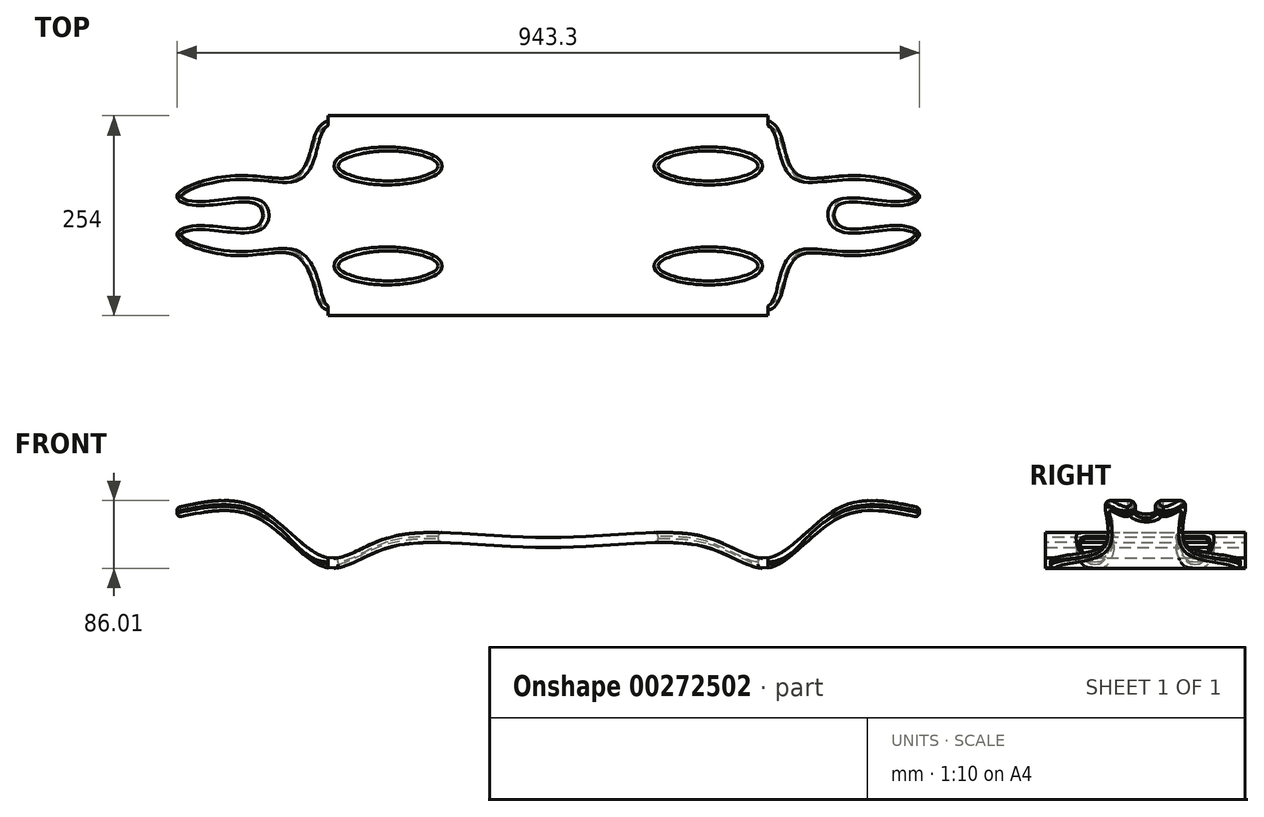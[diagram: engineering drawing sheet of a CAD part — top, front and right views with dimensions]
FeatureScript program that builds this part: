
annotation { "Feature Type Name" : "Feature", "Feature Type Description" : "" }
export const myFeature = defineFeature(function(context is Context, id is Id, definition is map)
    precondition{}
    {
        {
            var Q0;
            Q0=qCreatedBy(makeId("Front.planeOp"),FACE);
            var sketch = newSketch(context, id + "F0", { "sketchPlane" : qUnion([Q0])});
            skPoint(sketch, "E0.middle", {"position": v(0, 0) * mm});
            skLineSegment(sketch, "E1.right", {"start": v(-471.71, 57.15) * mm, "end": v(-471.71, 69.85) * mm});
            skLineSegment(sketch, "E2", {"start": v(-471.71, 69.85) * mm, "end": v(-471.71, 57.15) * mm});
            skLineSegment(sketch, "E3", {"start": v(471.71, 57.15) * mm, "end": v(471.71, 69.85) * mm});
            skPoint(sketch, "E4.endSnap0", {"position": v(0, 6.35) * mm});
            skPoint(sketch, "E4.start.orphan", {"position": v(0, -6.35) * mm});
            skPoint(sketch, "E5.trimOffspring.end.orphan", {"position": v(0, 19.05) * mm});
            skPoint(sketch, "E6.start.orphan", {"position": v(228.6, 19.05) * mm});
            skPoint(sketch, "E7.end.orphan", {"position": v(-228.6, 19.05) * mm});
            skFitSpline(sketch, "E8", {"points": [v(-471.71, 57.15) * mm, v(-370.11, 57.15) * mm, v(-281.21, -6.35) * mm, v(-203.2, 19.05) * mm, v(0, 19.05) * mm, v(203.2, 19.05) * mm, v(281.21, -6.35) * mm, v(370.11, 57.15) * mm, v(471.71, 57.15) * mm], "startDerivative": vector(913.94, 203.4) * mm, "endDerivative": vector(913.94, -203.4) * mm});
            skFitSpline(sketch, "E9", {"points": [v(471.71, 69.85) * mm, v(370.11, 69.85) * mm, v(281.21, 6.35) * mm, v(203.2, 31.75) * mm, v(0, 31.75) * mm, v(-203.2, 31.75) * mm, v(-281.21, 6.35) * mm, v(-370.11, 69.85) * mm, v(-471.71, 69.85) * mm], "startDerivative": vector(-913.94, 203.4) * mm, "endDerivative": vector(-913.94, -203.4) * mm});
            skPoint(sketch, "E0.right.end.orphan", {"position": v(-319.31, -6.35) * mm});
            skPoint(sketch, "E0.right.start.orphan", {"position": v(-319.31, 6.35) * mm});
            skSolve(sketch);
        }
        {
            var Q0;
            Q0 = qSketchRegion(id + "F0", true);
            extrude(context, id + "F1", {"entities" : qUnion([Q0]), "depth" : 127 * mm, "offsetDistance" : 25.4 * mm, "hasSecondDirection" : true, "secondDirectionOppositeDirection" : true, "secondDirectionDepth" : 127 * mm});
        }
        {
            var Q0;
            Q0=qCreatedBy(makeId("Top.planeOp"),FACE);
            var sketch = newSketch(context, id + "F2", { "sketchPlane" : qUnion([Q0])});
            skLineSegment(sketch, "E10.bottom", {"start": v(473.08, 127) * mm, "end": v(-473.07, 127) * mm});
            skLineSegment(sketch, "E10.top", {"start": v(473.07, -127) * mm, "end": v(-473.08, -127) * mm});
            skLineSegment(sketch, "E10.left", {"start": v(473.08, 127) * mm, "end": v(473.08, 50.8) * mm});
            skLineSegment(sketch, "E10.right", {"start": v(-473.08, 127) * mm, "end": v(-473.08, -127) * mm});
            skPoint(sketch, "E10.middle", {"position": v(0, 0) * mm});
            skLineSegment(sketch, "E11", {"start": v(-364.02, 0) * mm, "end": v(369.89, 0) * mm});
            skLineSegment(sketch, "E12", {"start": v(0, 101.2) * mm, "end": v(0, -101.6) * mm});
            skLineSegment(sketch, "E13", {"start": v(-473.08, 50.8) * mm, "end": v(-473.08, -50.8) * mm});
            skLineSegment(sketch, "E14", {"start": v(473.07, -50.8) * mm, "end": v(473.07, 50.8) * mm});
            skLineSegment(sketch, "E15.trimOffspring", {"start": v(473.08, -50.8) * mm, "end": v(473.08, -127) * mm});
            skLineSegment(sketch, "E16.left", {"start": v(473.07, 50.8) * mm, "end": v(473.07, -50.8) * mm});
            skLineSegment(sketch, "E16.right", {"start": v(319.09, 50.8) * mm, "end": v(319.09, -50.8) * mm});
            skLineSegment(sketch, "E17.left", {"start": v(-473.08, -50.8) * mm, "end": v(-473.08, 50.8) * mm});
            skLineSegment(sketch, "E17.right", {"start": v(-320.67, -50.8) * mm, "end": v(-320.67, 50.8) * mm});
            skLineSegment(sketch, "E18", {"start": v(-279.4, -127) * mm, "end": v(279.4, -127) * mm});
            skLineSegment(sketch, "E19.top", {"start": v(-279.4, 127) * mm, "end": v(279.4, 127) * mm});
            skLineSegment(sketch, "E19.left", {"start": v(-279.4, -102) * mm, "end": v(-279.4, 101.2) * mm});
            skLineSegment(sketch, "E19.right", {"start": v(279.4, -120.65) * mm, "end": v(279.4, 101.2) * mm});
            skLineSegment(sketch, "E20", {"start": v(-473.08, 0) * mm, "end": v(-473.08, 50.8) * mm});
            skLineSegment(sketch, "E21", {"start": v(-473.08, 0) * mm, "end": v(-473.08, -50.8) * mm});
            skLineSegment(sketch, "E22", {"start": v(473.07, -50.8) * mm, "end": v(473.07, 0) * mm});
            skLineSegment(sketch, "E23", {"start": v(473.08, 0) * mm, "end": v(473.08, 50.8) * mm});
            skLineSegment(sketch, "E24.left", {"start": v(-473.07, -13.1) * mm, "end": v(-473.08, 12.3) * mm});
            skPoint(sketch, "E24.middle", {"position": v(-420.69, 0) * mm});
            skLineSegment(sketch, "E25.left", {"start": v(473.08, -13.1) * mm, "end": v(471.49, 12.7) * mm});
            skPoint(sketch, "E25.middle", {"position": v(420.69, 0) * mm});
            skPoint(sketch, "E26.end.orphan", {"position": v(0, -127) * mm});
            skPoint(sketch, "E27.end.orphan", {"position": v(0, 127) * mm});
            skLineSegment(sketch, "E28", {"start": v(-279.4, -127) * mm, "end": v(-279.4, -120.65) * mm});
            skLineSegment(sketch, "E29", {"start": v(-279.4, -120.65) * mm, "end": v(-279.4, -127) * mm});
            skLineSegment(sketch, "E30", {"start": v(-279.4, 127) * mm, "end": v(-279.4, 120.65) * mm});
            skLineSegment(sketch, "E31", {"start": v(-279.4, 120.65) * mm, "end": v(-279.4, 127) * mm});
            skLineSegment(sketch, "E32", {"start": v(279.4, 120.65) * mm, "end": v(279.4, 127) * mm});
            skLineSegment(sketch, "E33", {"start": v(279.4, -120.65) * mm, "end": v(279.4, -127) * mm});
            skFitSpline(sketch, "E34", {"points": [v(319.09, -50.8) * mm, v(396.08, -50.8) * mm, v(471.49, -25.4) * mm, v(446.09, -12.7) * mm, v(369.89, -12.7) * mm, v(368.3, 13.1) * mm, v(446.09, 12.7) * mm, v(471.49, 25.4) * mm, v(396.08, 50.8) * mm, v(319.09, 50.8) * mm, v(299.24, 88.9) * mm, v(279.4, 120.65) * mm, v(0, 101.2) * mm, v(-279.4, 120.65) * mm, v(-300.04, 88.9) * mm, v(-320.67, 50.8) * mm, v(-396.88, 50.8) * mm, v(-471.49, 25.4) * mm, v(-446.09, 12.7) * mm, v(-368.3, 13.1) * mm, v(-368.3, -12.3) * mm, v(-446.09, -12.7) * mm, v(-471.49, -25.4) * mm, v(-396.88, -50.8) * mm, v(-320.67, -50.8) * mm, v(-295.64, -95.82) * mm, v(-279.4, -120.65) * mm, v(0, -101.6) * mm, v(279.4, -120.65) * mm, v(299.24, -88.9) * mm, v(319.09, -50.8) * mm]});
            skLineSegment(sketch, "E35.bottom", {"start": v(279.4, 101.2) * mm, "end": v(-279.4, 101.2) * mm});
            skLineSegment(sketch, "E35.top", {"start": v(279.4, -102) * mm, "end": v(-279.4, -102) * mm});
            skLineSegment(sketch, "E35.left", {"start": v(279.4, 101.2) * mm, "end": v(279.4, -102) * mm});
            skLineSegment(sketch, "E35.right", {"start": v(-279.4, 101.2) * mm, "end": v(-279.4, -102) * mm});
            skLineSegment(sketch, "E36.bottom", {"start": v(-279.4, -102) * mm, "end": v(-266.7, -102) * mm});
            skLineSegment(sketch, "E36.top", {"start": v(-279.4, -82.96) * mm, "end": v(-266.7, -82.96) * mm});
            skLineSegment(sketch, "E36.left", {"start": v(-279.4, -102) * mm, "end": v(-279.4, -82.96) * mm});
            skLineSegment(sketch, "E36.right", {"start": v(-266.7, -102) * mm, "end": v(-266.7, -82.96) * mm});
            skLineSegment(sketch, "E37.bottom", {"start": v(-279.4, 101.2) * mm, "end": v(-266.7, 101.2) * mm});
            skLineSegment(sketch, "E37.top", {"start": v(-279.4, 82.14) * mm, "end": v(-266.7, 82.14) * mm});
            skLineSegment(sketch, "E37.left", {"start": v(-279.4, 101.2) * mm, "end": v(-279.4, 82.14) * mm});
            skLineSegment(sketch, "E37.right", {"start": v(-266.7, 101.2) * mm, "end": v(-266.7, 82.14) * mm});
            skLineSegment(sketch, "E38.bottom", {"start": v(279.4, 101.2) * mm, "end": v(266.7, 101.2) * mm});
            skLineSegment(sketch, "E38.top", {"start": v(279.4, 82.14) * mm, "end": v(266.7, 82.14) * mm});
            skLineSegment(sketch, "E38.left", {"start": v(279.4, 101.2) * mm, "end": v(279.4, 82.14) * mm});
            skLineSegment(sketch, "E38.right", {"start": v(266.7, 101.2) * mm, "end": v(266.7, 82.14) * mm});
            skLineSegment(sketch, "E39.bottom", {"start": v(279.4, -102) * mm, "end": v(266.7, -102) * mm});
            skLineSegment(sketch, "E39.top", {"start": v(279.4, -82.96) * mm, "end": v(266.7, -82.96) * mm});
            skLineSegment(sketch, "E39.left", {"start": v(279.4, -102) * mm, "end": v(279.4, -82.96) * mm});
            skLineSegment(sketch, "E39.right", {"start": v(266.7, -102) * mm, "end": v(266.7, -82.96) * mm});
            skLineSegment(sketch, "E40", {"start": v(-266.7, -82.96) * mm, "end": v(-266.7, -44.86) * mm});
            skLineSegment(sketch, "E41", {"start": v(-266.7, 82.14) * mm, "end": v(-266.7, 44.04) * mm});
            skLineSegment(sketch, "E42", {"start": v(266.7, -82.96) * mm, "end": v(266.7, -44.86) * mm});
            skLineSegment(sketch, "E43", {"start": v(266.7, 82.14) * mm, "end": v(266.7, 44.04) * mm});
            skLineSegment(sketch, "E44.bottom", {"start": v(-266.7, -44.86) * mm, "end": v(-139.7, -44.86) * mm});
            skLineSegment(sketch, "E44.top", {"start": v(-266.7, -82.96) * mm, "end": v(-139.7, -82.96) * mm});
            skLineSegment(sketch, "E44.left", {"start": v(-266.7, -44.86) * mm, "end": v(-266.7, -82.96) * mm});
            skLineSegment(sketch, "E44.right", {"start": v(-139.7, -44.86) * mm, "end": v(-139.7, -82.96) * mm});
            skLineSegment(sketch, "E45.bottom", {"start": v(-266.7, 82.14) * mm, "end": v(-139.7, 82.14) * mm});
            skLineSegment(sketch, "E45.top", {"start": v(-266.7, 44.04) * mm, "end": v(-139.7, 44.04) * mm});
            skLineSegment(sketch, "E45.right", {"start": v(-139.7, 82.14) * mm, "end": v(-139.7, 44.04) * mm});
            skLineSegment(sketch, "E46.bottom", {"start": v(266.7, 82.14) * mm, "end": v(139.7, 82.14) * mm});
            skLineSegment(sketch, "E46.top", {"start": v(266.7, 44.04) * mm, "end": v(139.7, 44.04) * mm});
            skLineSegment(sketch, "E46.right", {"start": v(139.7, 82.14) * mm, "end": v(139.7, 44.04) * mm});
            skLineSegment(sketch, "E47.bottom", {"start": v(266.7, -82.96) * mm, "end": v(139.7, -82.96) * mm});
            skLineSegment(sketch, "E47.top", {"start": v(266.7, -44.86) * mm, "end": v(139.7, -44.86) * mm});
            skLineSegment(sketch, "E47.right", {"start": v(139.7, -82.96) * mm, "end": v(139.7, -44.86) * mm});
            skFitSpline(sketch, "E48", {"points": [v(-266.7, 63.1) * mm, v(-203.2, 44.04) * mm, v(-139.7, 63.1) * mm, v(-203.2, 82.14) * mm, v(-266.7, 63.1) * mm]});
            skFitSpline(sketch, "E49", {"points": [v(-266.7, -63.9) * mm, v(-203.2, -82.96) * mm, v(-139.7, -63.9) * mm, v(-203.2, -44.86) * mm, v(-266.7, -63.9) * mm]});
            skFitSpline(sketch, "E50", {"points": [v(139.7, -63.9) * mm, v(203.2, -82.96) * mm, v(266.7, -63.9) * mm, v(203.2, -44.86) * mm, v(139.7, -63.9) * mm]});
            skFitSpline(sketch, "E51", {"points": [v(139.7, 63.1) * mm, v(203.2, 44.04) * mm, v(266.7, 63.1) * mm, v(203.2, 82.14) * mm, v(139.7, 63.1) * mm]});
            skSolve(sketch);
        }
        {
            var Q0;
            {var subQ5=sQuery(id+"F2.wireOp",EDGE,"E15.trimOffspring");Q0=makeQuery(id+"F2.imprint","IMPRINT",FACE,{"disambiguationData":[TD([[makeQuery(id+"F2.imprint","IMPRINT",EDGE,{"derivedFrom":subQ5}),-1.0]])]});}
            var Q1;
            {var subQ4=sQuery(id+"F2.wireOp",EDGE,"E25.left");Q1=makeQuery(id+"F2.imprint","IMPRINT",FACE,{"disambiguationData":[TD([[makeQuery(id+"F2.imprint","IMPRINT",EDGE,{"derivedFrom":subQ4}),1.0]])]});}
            var Q2;
            {var subQ0=sQuery(id+"F2.wireOp",EDGE,"e9d015ac-fda8-45dd-bf0b-8d8da068c592");var subQ1=sQuery(id+"F2.wireOp",EDGE,"E19.top");var subQ2=makeQuery(id+"F2.imprint","INTERSECT",VERTEX,{"disambiguationData":[OD(0.0)],"derivedFrom":[subQ1,subQ0]});Q2=makeQuery(id+"F2.imprint","IMPRINT",FACE,{"disambiguationData":[TD([[makeQuery(id+"F2.imprint","IMPRINT",EDGE,{"disambiguationData":[TD([[subQ2,-1.0]])],"derivedFrom":subQ1}),-1.0]])]});}
            var Q3;
            {var subQ0=sQuery(id+"F2.wireOp",EDGE,"e9d015ac-fda8-45dd-bf0b-8d8da068c592");var subQ1=sQuery(id+"F2.wireOp",EDGE,"E18");var subQ2=makeQuery(id+"F2.imprint","INTERSECT",VERTEX,{"disambiguationData":[OD(0.0)],"derivedFrom":[subQ1,subQ0]});Q3=makeQuery(id+"F2.imprint","IMPRINT",FACE,{"disambiguationData":[TD([[makeQuery(id+"F2.imprint","IMPRINT",EDGE,{"disambiguationData":[TD([[subQ2,-1.0]])],"derivedFrom":subQ1}),1.0]])]});}
            var Q4;
            {var subQ4=sQuery(id+"F2.wireOp",EDGE,"E10.right");var subQ6=sQuery(id+"F2.wireOp",EDGE,"E10.top");var subQ7=makeQuery(id+"F2.imprint","INTERSECT",VERTEX,{"derivedFrom":[subQ6,subQ4]});Q4=makeQuery(id+"F2.imprint","IMPRINT",FACE,{"disambiguationData":[TD([[makeQuery(id+"F2.imprint","IMPRINT",EDGE,{"disambiguationData":[TD([[subQ7,1.0]])],"derivedFrom":subQ4}),1.0]])]});}
            var Q5;
            {var subQ4=sQuery(id+"F2.wireOp",EDGE,"E24.left");Q5=makeQuery(id+"F2.imprint","IMPRINT",FACE,{"disambiguationData":[TD([[makeQuery(id+"F2.imprint","IMPRINT",EDGE,{"derivedFrom":subQ4}),-1.0]])]});}
            var Q6;
            {var subQ1=sQuery(id+"F2.wireOp",EDGE,"E10.right");var subQ5=sQuery(id+"F2.wireOp",EDGE,"E10.bottom");var subQ6=makeQuery(id+"F2.imprint","INTERSECT",VERTEX,{"derivedFrom":[subQ5,subQ1]});Q6=makeQuery(id+"F2.imprint","IMPRINT",FACE,{"disambiguationData":[TD([[makeQuery(id+"F2.imprint","IMPRINT",EDGE,{"disambiguationData":[TD([[subQ6,-1.0]])],"derivedFrom":subQ1}),1.0]])]});}
            var Q7;
            {var subQ1=sQuery(id+"F2.wireOp",EDGE,"E10.left");Q7=makeQuery(id+"F2.imprint","IMPRINT",FACE,{"disambiguationData":[TD([[makeQuery(id+"F2.imprint","IMPRINT",EDGE,{"derivedFrom":subQ1}),-1.0]])]});}
            extrude(context, id + "F3", {"entities" : qUnion([Q0, Q1, Q2, Q3, Q4, Q5, Q6, Q7]), "operationType" : NewBodyOperationType.REMOVE, "depth" : 127 * mm, "offsetDistance" : 25.4 * mm, "hasSecondDirection" : true, "secondDirectionOppositeDirection" : true, "secondDirectionDepth" : 25.4 * mm});
        }
        {
            var Q0;
            {var subQ0=sQuery(id+"F2.wireOp",EDGE,"E49");var subQ1=makeQuery(id+"F2.imprint","INTERSECT",VERTEX,{"derivedFrom":[sQuery(id+"F2.wireOp",EDGE,"E44.top"),subQ0]});Q0=makeQuery(id+"F2.imprint","IMPRINT",FACE,{"disambiguationData":[TD([[makeQuery(id+"F2.imprint","IMPRINT",EDGE,{"disambiguationData":[TD([[subQ1,1.0]])],"derivedFrom":subQ0}),1.0]])]});}
            var Q1;
            {var subQ0=sQuery(id+"F2.wireOp",EDGE,"E48");var subQ1=makeQuery(id+"F2.imprint","INTERSECT",VERTEX,{"derivedFrom":[sQuery(id+"F2.wireOp",EDGE,"E45.top"),subQ0]});Q1=makeQuery(id+"F2.imprint","IMPRINT",FACE,{"disambiguationData":[TD([[makeQuery(id+"F2.imprint","IMPRINT",EDGE,{"disambiguationData":[TD([[subQ1,1.0]])],"derivedFrom":subQ0}),1.0]])]});}
            var Q2;
            {var subQ0=sQuery(id+"F2.wireOp",EDGE,"E51");var subQ1=makeQuery(id+"F2.imprint","INTERSECT",VERTEX,{"derivedFrom":[sQuery(id+"F2.wireOp",EDGE,"E46.top"),subQ0]});Q2=makeQuery(id+"F2.imprint","IMPRINT",FACE,{"disambiguationData":[TD([[makeQuery(id+"F2.imprint","IMPRINT",EDGE,{"disambiguationData":[TD([[subQ1,1.0]])],"derivedFrom":subQ0}),1.0]])]});}
            var Q3;
            {var subQ0=sQuery(id+"F2.wireOp",EDGE,"E50");var subQ1=makeQuery(id+"F2.imprint","INTERSECT",VERTEX,{"derivedFrom":[sQuery(id+"F2.wireOp",EDGE,"E47.bottom"),subQ0]});Q3=makeQuery(id+"F2.imprint","IMPRINT",FACE,{"disambiguationData":[TD([[makeQuery(id+"F2.imprint","IMPRINT",EDGE,{"disambiguationData":[TD([[subQ1,1.0]])],"derivedFrom":subQ0}),1.0]])]});}
            extrude(context, id + "F4", {"entities" : qUnion([Q0, Q1, Q2, Q3]), "operationType" : NewBodyOperationType.REMOVE, "depth" : 50.8 * mm, "offsetDistance" : 25.4 * mm, "hasSecondDirection" : true, "secondDirectionOppositeDirection" : true, "secondDirectionDepth" : 25.4 * mm});
        }
        {
            var Q0;
            Q0=makeQuery(id+"F3.boolean.opBoolean","INTERSECT",EDGE,{"derivedFrom":[makeQuery(id+"F1.opExtrude","SWEPT_FACE",FACE,{"disambiguationData":[OSD([sQuery(id+"F0.wireOp",EDGE,"E9")])]}),makeQuery(id+"F3.opExtrude","SWEPT_FACE",FACE,{"disambiguationData":[OSD([sQuery(id+"F2.wireOp",EDGE,"E34")])]})]});
            var Q1;
            Q1=makeQuery(id+"F3.boolean.opBoolean","INTERSECT",EDGE,{"derivedFrom":[makeQuery(id+"F1.opExtrude","SWEPT_FACE",FACE,{"disambiguationData":[OSD([sQuery(id+"F0.wireOp",EDGE,"E8")])]}),makeQuery(id+"F3.opExtrude","SWEPT_FACE",FACE,{"disambiguationData":[OSD([sQuery(id+"F2.wireOp",EDGE,"E34")])]})]});
            var Q2;
            Q2=makeQuery(id+"F3.boolean.opBoolean","INTERSECT",EDGE,{"derivedFrom":[makeQuery(id+"F1.opExtrude","SWEPT_FACE",FACE,{"disambiguationData":[OSD([sQuery(id+"F0.wireOp",EDGE,"E9")])]}),makeQuery(id+"F3.opExtrude","SWEPT_FACE",FACE,{"disambiguationData":[OSD([sQuery(id+"F2.wireOp",EDGE,"E35.top")])]})]});
            var Q3;
            Q3=makeQuery(id+"F3.boolean.opBoolean","INTERSECT",EDGE,{"derivedFrom":[makeQuery(id+"F1.opExtrude","SWEPT_FACE",FACE,{"disambiguationData":[OSD([sQuery(id+"F0.wireOp",EDGE,"E8")])]}),makeQuery(id+"F3.opExtrude","SWEPT_FACE",FACE,{"disambiguationData":[OSD([sQuery(id+"F2.wireOp",EDGE,"E35.top")])]})]});
            fillet(context, id + "F5", {"entities" : qUnion([Q0, Q1, Q2, Q3]), "radius" : 5.08 * mm, "tangentPropagation" : true, "allowEdgeOverflow" : false});
        }
        {
            var Q0;
            Q0=makeQuery(id+"F4.boolean.opBoolean","INTERSECT",EDGE,{"derivedFrom":[makeQuery(id+"F1.opExtrude","SWEPT_FACE",FACE,{"disambiguationData":[OSD([sQuery(id+"F0.wireOp",EDGE,"E9")])]}),makeQuery(id+"F4.opExtrude","SWEPT_FACE",FACE,{"disambiguationData":[OSD([sQuery(id+"F2.wireOp",EDGE,"E51")])]})]});
            var Q1;
            Q1=makeQuery(id+"F4.boolean.opBoolean","INTERSECT",EDGE,{"derivedFrom":[makeQuery(id+"F1.opExtrude","SWEPT_FACE",FACE,{"disambiguationData":[OSD([sQuery(id+"F0.wireOp",EDGE,"E8")])]}),makeQuery(id+"F4.opExtrude","SWEPT_FACE",FACE,{"disambiguationData":[OSD([sQuery(id+"F2.wireOp",EDGE,"E51")])]})]});
            var Q2;
            Q2=makeQuery(id+"F4.boolean.opBoolean","INTERSECT",EDGE,{"derivedFrom":[makeQuery(id+"F1.opExtrude","SWEPT_FACE",FACE,{"disambiguationData":[OSD([sQuery(id+"F0.wireOp",EDGE,"E9")])]}),makeQuery(id+"F4.opExtrude","SWEPT_FACE",FACE,{"disambiguationData":[OSD([sQuery(id+"F2.wireOp",EDGE,"E50")])]})]});
            var Q3;
            Q3=makeQuery(id+"F4.boolean.opBoolean","INTERSECT",EDGE,{"derivedFrom":[makeQuery(id+"F1.opExtrude","SWEPT_FACE",FACE,{"disambiguationData":[OSD([sQuery(id+"F0.wireOp",EDGE,"E8")])]}),makeQuery(id+"F4.opExtrude","SWEPT_FACE",FACE,{"disambiguationData":[OSD([sQuery(id+"F2.wireOp",EDGE,"E50")])]})]});
            fillet(context, id + "F6", {"entities" : qUnion([Q0, Q1, Q2, Q3]), "radius" : 5.08 * mm, "tangentPropagation" : true, "allowEdgeOverflow" : false});
        }
        {
            var Q0;
            Q0=makeQuery(id+"F4.boolean.opBoolean","INTERSECT",EDGE,{"derivedFrom":[makeQuery(id+"F1.opExtrude","SWEPT_FACE",FACE,{"disambiguationData":[OSD([sQuery(id+"F0.wireOp",EDGE,"E9")])]}),makeQuery(id+"F4.opExtrude","SWEPT_FACE",FACE,{"disambiguationData":[OSD([sQuery(id+"F2.wireOp",EDGE,"E48")])]})]});
            var Q1;
            Q1=makeQuery(id+"F4.boolean.opBoolean","INTERSECT",EDGE,{"derivedFrom":[makeQuery(id+"F1.opExtrude","SWEPT_FACE",FACE,{"disambiguationData":[OSD([sQuery(id+"F0.wireOp",EDGE,"E8")])]}),makeQuery(id+"F4.opExtrude","SWEPT_FACE",FACE,{"disambiguationData":[OSD([sQuery(id+"F2.wireOp",EDGE,"E48")])]})]});
            var Q2;
            Q2=makeQuery(id+"F4.boolean.opBoolean","INTERSECT",EDGE,{"derivedFrom":[makeQuery(id+"F1.opExtrude","SWEPT_FACE",FACE,{"disambiguationData":[OSD([sQuery(id+"F0.wireOp",EDGE,"E9")])]}),makeQuery(id+"F4.opExtrude","SWEPT_FACE",FACE,{"disambiguationData":[OSD([sQuery(id+"F2.wireOp",EDGE,"E49")])]})]});
            var Q3;
            Q3=makeQuery(id+"F4.boolean.opBoolean","INTERSECT",EDGE,{"derivedFrom":[makeQuery(id+"F1.opExtrude","SWEPT_FACE",FACE,{"disambiguationData":[OSD([sQuery(id+"F0.wireOp",EDGE,"E8")])]}),makeQuery(id+"F4.opExtrude","SWEPT_FACE",FACE,{"disambiguationData":[OSD([sQuery(id+"F2.wireOp",EDGE,"E49")])]})]});
            fillet(context, id + "F7", {"entities" : qUnion([Q0, Q1, Q2, Q3]), "radius" : 5.08 * mm, "tangentPropagation" : true, "allowEdgeOverflow" : false});
        }
    });
